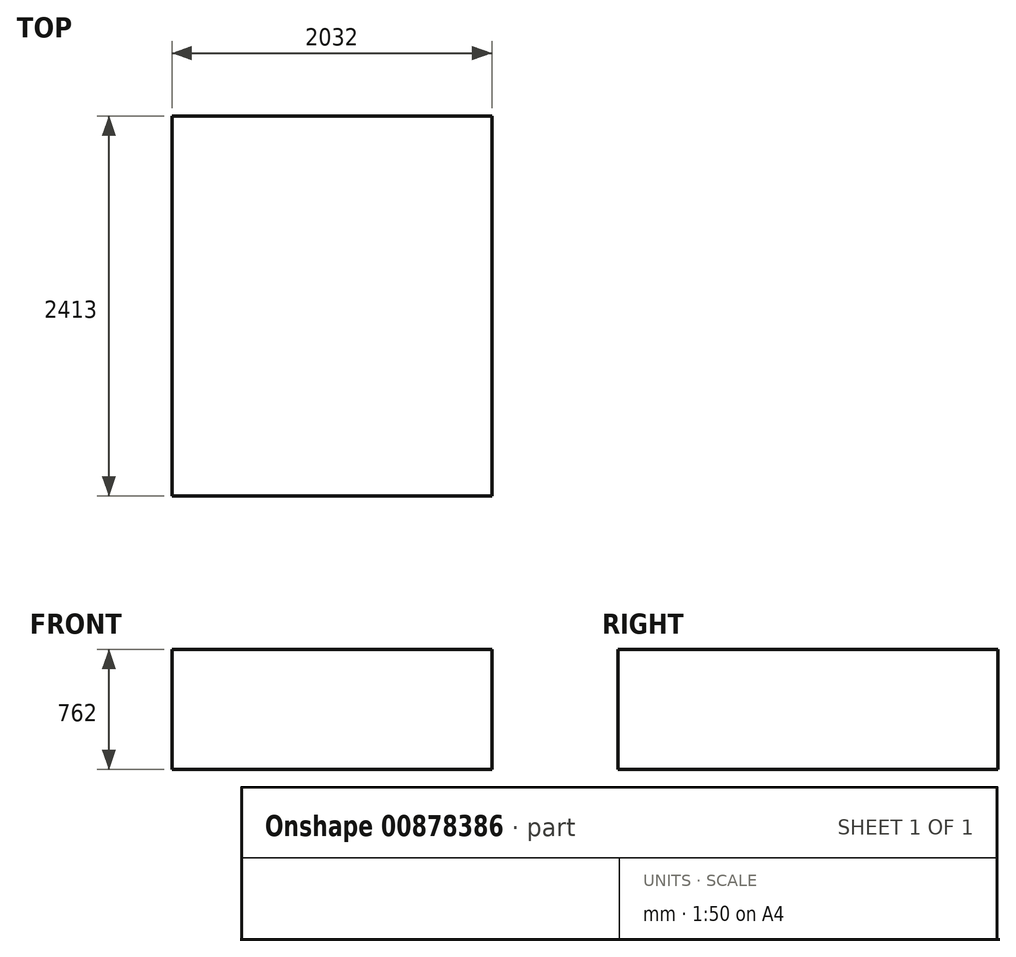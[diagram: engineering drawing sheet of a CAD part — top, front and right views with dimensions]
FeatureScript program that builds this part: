
annotation { "Feature Type Name" : "Feature", "Feature Type Description" : "" }
export const myFeature = defineFeature(function(context is Context, id is Id, definition is map)
    precondition{}
    {
        {
            var Q0;
            Q0=qCreatedBy(makeId("Top.planeOp"),FACE);
            var sketch = newSketch(context, id + "F0", { "sketchPlane" : qUnion([Q0])});
            skLineSegment(sketch, "E0.bottom", {"start": v(2743.2, 2336.3) * mm, "end": v(-2743.2, 2336.3) * mm});
            skLineSegment(sketch, "E0.top", {"start": v(2743.2, -2336.3) * mm, "end": v(-2743.2, -2336.3) * mm});
            skLineSegment(sketch, "E0.left", {"start": v(2743.2, 2336.3) * mm, "end": v(2743.2, -2336.3) * mm});
            skLineSegment(sketch, "E0.right", {"start": v(-2743.2, 2336.3) * mm, "end": v(-2743.2, -2336.3) * mm});
            skPoint(sketch, "E0.middle", {"position": v(0, 0) * mm});
            skSolve(sketch);
        }
        {
            var Q0;
            Q0=makeQuery(id+"F0.imprint","IMPRINT",FACE,{"disambiguationData":[TD([[makeQuery(id+"F0.imprint","IMPRINT",EDGE,{"derivedFrom":sQuery(id+"F0.wireOp",EDGE,"E0.bottom")}),1.0]])]});
            var sketch = newSketch(context, id + "F1", { "sketchPlane" : qUnion([Q0])});
            skLineSegment(sketch, "E1.bottom", {"start": v(-2286, 1295.4) * mm, "end": v(2286, 1295.4) * mm});
            skLineSegment(sketch, "E1.top", {"start": v(-2286, -1295.4) * mm, "end": v(2286, -1295.4) * mm});
            skLineSegment(sketch, "E1.left", {"start": v(-2286, 1295.4) * mm, "end": v(-2286, -1295.4) * mm});
            skLineSegment(sketch, "E1.right", {"start": v(2286, 1295.4) * mm, "end": v(2286, -1295.4) * mm});
            skPoint(sketch, "E1.middle", {"position": v(0, 0) * mm});
            skSolve(sketch);
        }
        {
            var Q0;
            Q0=makeQuery(id+"F1.imprint","IMPRINT",FACE,{"disambiguationData":[TD([[makeQuery(id+"F1.imprint","IMPRINT",EDGE,{"derivedFrom":sQuery(id+"F1.wireOp",EDGE,"E1.bottom")}),1.0]])]});
            var sketch = newSketch(context, id + "F2", { "sketchPlane" : qUnion([Q0])});
            skLineSegment(sketch, "E2", {"start": v(-2729.7, -2327.3) * mm, "end": v(-2018.5, -2327.3) * mm});
            skLineSegment(sketch, "E3.bottom", {"start": v(-2018.5, -2327.3) * mm, "end": v(13.5, -2327.3) * mm});
            skLineSegment(sketch, "E3.top", {"start": v(-2018.5, 85.7) * mm, "end": v(13.5, 85.7) * mm});
            skLineSegment(sketch, "E3.left", {"start": v(-2018.5, -2327.3) * mm, "end": v(-2018.5, 85.7) * mm});
            skLineSegment(sketch, "E3.right", {"start": v(13.5, -2327.3) * mm, "end": v(13.5, 85.7) * mm});
            skSolve(sketch);
        }
        {
            var Q0;
            Q0 = qSketchRegion(id + "F2", true);
            extrude(context, id + "F3", {"entities" : qUnion([Q0]), "depth" : 762 * mm, "offsetDistance" : 25.4 * mm});
        }
    });
